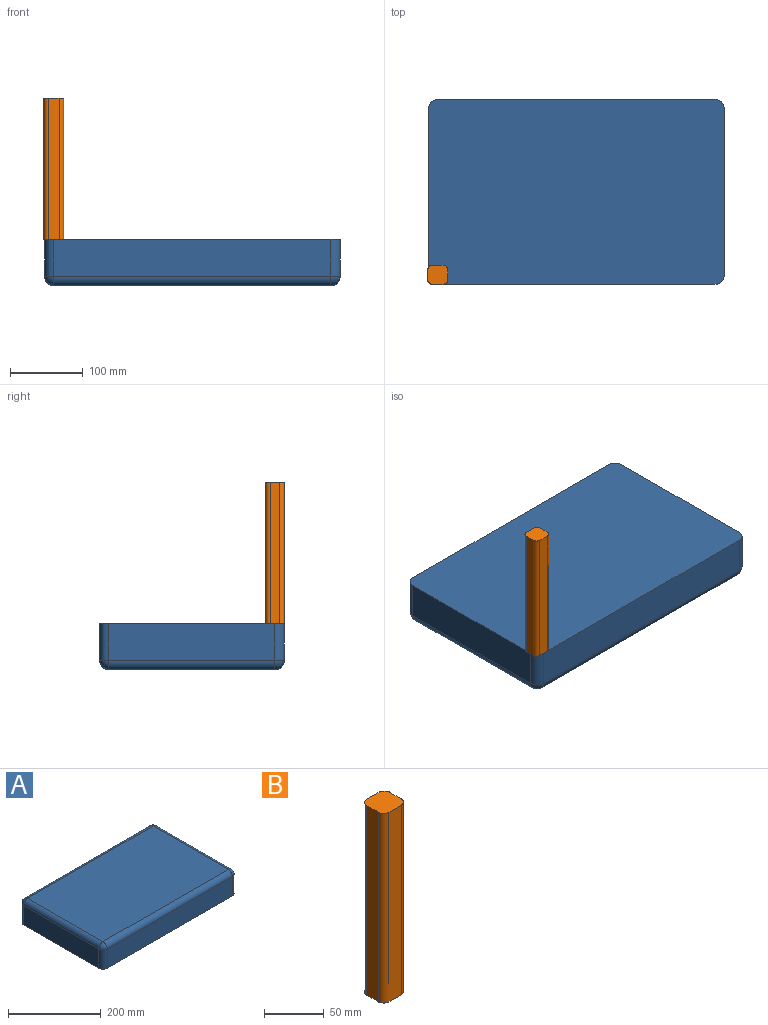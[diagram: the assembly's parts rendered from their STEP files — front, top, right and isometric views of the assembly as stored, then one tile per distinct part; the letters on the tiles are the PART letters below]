
ASSEMBLY  parts=2 mates=1
PART A: 18 faces, bbox 406.4x254x63.5 mm
  f0: plane 381x50.8mm, normal (0,-1,0), area 19354.8mm2, adj f5,f6,f7,f13
  f1: plane 228.6x50.8mm, normal (1,0,0), area 11612.9mm2, adj f5,f6,f9,f10
  f2: plane 381x50.8mm, normal (0,1,0), area 19354.8mm2, adj f5,f10,f12,f17
  f3: plane 228.6x50.8mm, normal (-1,0,0), area 11612.9mm2, adj f5,f13,f15,f17
  f4: plane 381x228.6mm, normal (0,0,1), area 87096.6mm2, adj f7,f9,f12,f15
  f5: plane 406.4x254mm, normal (0,0,-1), area 103087.1mm2, adj f0,f1,f2,f3,f6,f10,f13,f17
  f6: cylinder r=12.7mm len=50.8mm, axis (0,0,-1), area 1013.4mm2, adj f0,f1,f5,f8
  f7: cylinder r=12.7mm len=381mm, axis (-1,0,0), area 7600.6mm2, adj f0,f4,f8,f14
  f8: sphere r=12.7mm, area 253.4mm2, adj f6,f7,f9
  f9: cylinder r=12.7mm len=228.6mm, axis (0,-1,0), area 4560.4mm2, adj f1,f4,f8,f11
  f10: cylinder r=12.7mm len=50.8mm, axis (0,0,1), area 1013.4mm2, adj f1,f2,f5,f11
  f11: sphere r=12.7mm, area 253.4mm2, adj f9,f10,f12
  f12: cylinder r=12.7mm len=381mm, axis (1,0,0), area 7600.6mm2, adj f2,f4,f11,f16
  f13: cylinder r=12.7mm len=50.8mm, axis (0,0,1), area 1013.4mm2, adj f0,f3,f5,f14
  f14: sphere r=12.7mm, area 253.4mm2, adj f7,f13,f15
  f15: cylinder r=12.7mm len=228.6mm, axis (0,1,0), area 4560.4mm2, adj f3,f4,f14,f16
  f16: sphere r=12.7mm, area 253.4mm2, adj f12,f15,f17
  f17: cylinder r=12.7mm len=50.8mm, axis (0,0,-1), area 1013.4mm2, adj f2,f3,f5,f16
PART B: 10 faces, bbox 27.2x26.3x194.1 mm
  f0: plane 194.07x14.48mm, normal (0,1,0), area 2809.7mm2, adj f1,f3,f7,f9
  f1: plane 27.18x26.3mm, normal (0,0,1), area 680.1mm2, adj f0,f2,f4,f5,f6,f7,f8,f9
  f2: plane 194.07x13.6mm, normal (-1,0,0), area 2638.6mm2, adj f1,f3,f8,f9
  f3: plane 27.18x26.3mm, normal (0,0,-1), area 680.1mm2, adj f0,f2,f4,f5,f6,f7,f8,f9
  f4: plane 194.07x13.6mm, normal (1,0,0), area 2638.6mm2, adj f1,f3,f6,f7
  f5: plane 194.07x14.48mm, normal (0,-1,0), area 2809.7mm2, adj f1,f3,f6,f8
  f6: cylinder r=6.35mm len=194.07mm, axis (0,0,1), area 1935.7mm2, adj f1,f3,f4,f5
  f7: cylinder r=6.35mm len=194.07mm, axis (0,0,-1), area 1935.7mm2, adj f0,f1,f3,f4
  f8: cylinder r=6.35mm len=194.07mm, axis (0,0,-1), area 1935.7mm2, adj f1,f2,f3,f5
  f9: cylinder r=6.35mm len=194.07mm, axis (0,0,1), area 1935.7mm2, adj f0,f1,f2,f3
PLACE A rot(axis=(1,0,0),180deg) t=(19.7,-107.28,-200.62)mm
PLACE B t=(-184.39,-211.8,-79.21)mm
MATE fastened A.f17 <-> B.f3  axis (0,0,1) through (-170.8,-221.58,-200.62)mm
